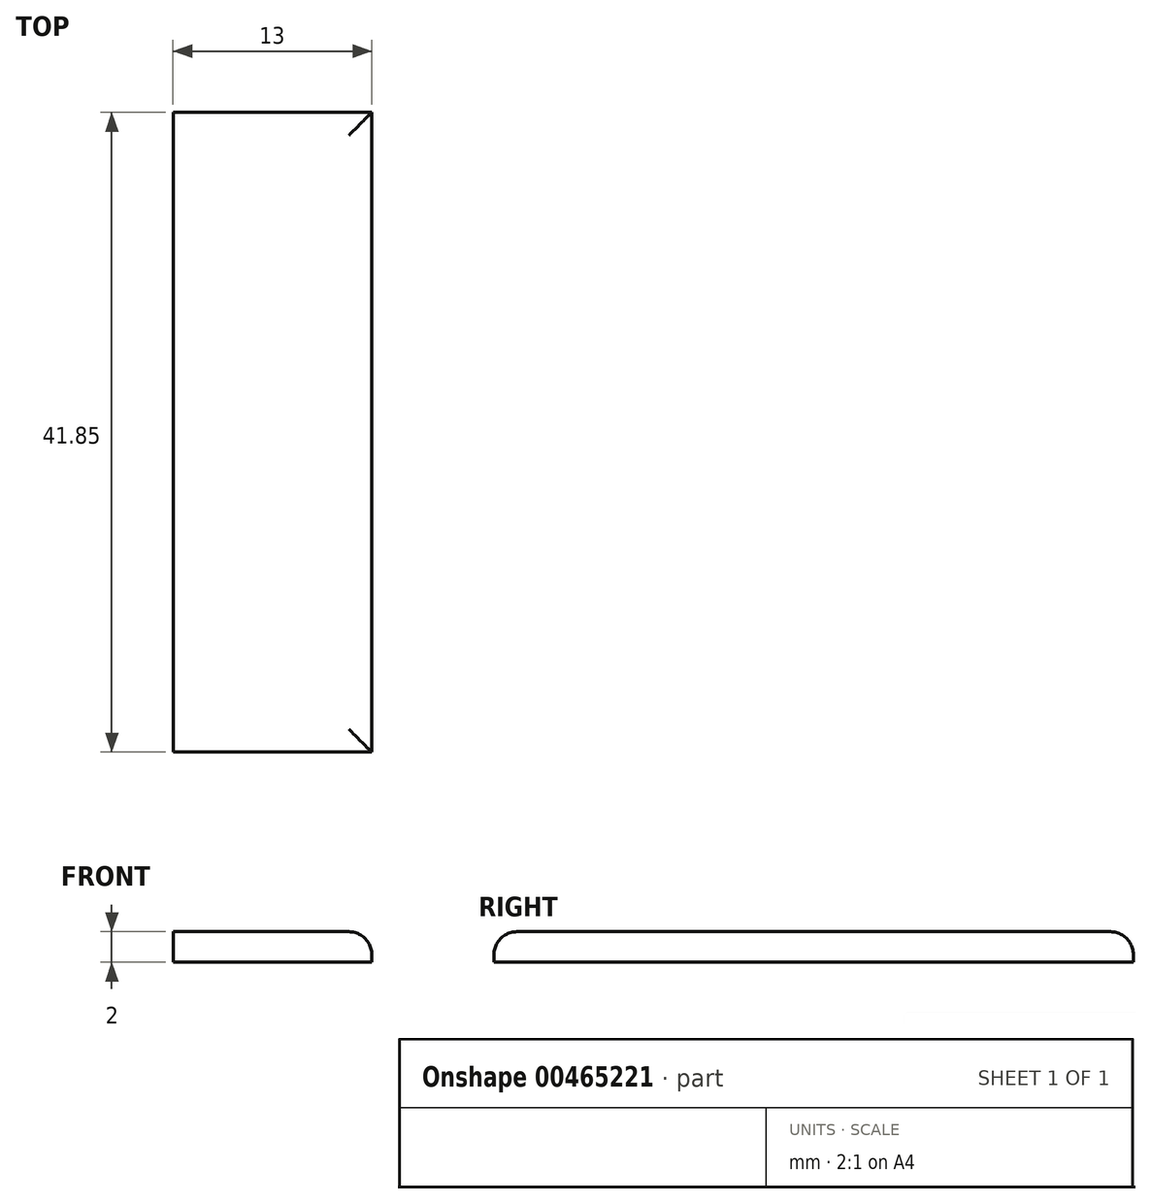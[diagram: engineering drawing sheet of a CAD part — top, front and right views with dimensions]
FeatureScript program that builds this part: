
annotation { "Feature Type Name" : "Feature", "Feature Type Description" : "" }
export const myFeature = defineFeature(function(context is Context, id is Id, definition is map)
    precondition{}
    {
        {
            var Q0;
            Q0=qCreatedBy(makeId("Top.planeOp"),FACE);
            var sketch = newSketch(context, id + "F0", { "sketchPlane" : qUnion([Q0])});
            skLineSegment(sketch, "E0.bottom", {"start": v(-8.26, 32.64) * mm, "end": v(4.74, 32.64) * mm});
            skLineSegment(sketch, "E0.top", {"start": v(-8.26, -9.2) * mm, "end": v(4.74, -9.2) * mm});
            skLineSegment(sketch, "E0.left", {"start": v(-8.26, 32.64) * mm, "end": v(-8.26, -9.2) * mm});
            skLineSegment(sketch, "E0.right", {"start": v(4.74, 32.64) * mm, "end": v(4.74, -9.2) * mm});
            skSolve(sketch);
        }
        {
            var Q0;
            Q0 = qSketchRegion(id + "F0", true);
            var Q1;
            Q1=makeQuery(id+"F0.imprint","IMPRINT",FACE,{"disambiguationData":[TD([[makeQuery(id+"F0.imprint","IMPRINT",EDGE,{"derivedFrom":sQuery(id+"F0.wireOp",EDGE,"E0.bottom")}),-1.0]])]});
            extrude(context, id + "F1", {"entities" : qUnion([Q0, Q1]), "depth" : 2 * mm});
        }
        {
            var Q0;
            Q0=makeQuery(id+"F1.opExtrude","CAP_EDGE",EDGE,{"disambiguationData":[OSD([sQuery(id+"F0.wireOp",EDGE,"E0.top")])],"isStart":false});
            var Q1;
            Q1=makeQuery(id+"F1.opExtrude","CAP_EDGE",EDGE,{"disambiguationData":[OSD([sQuery(id+"F0.wireOp",EDGE,"E0.right")])],"isStart":false});
            var Q2;
            Q2=makeQuery(id+"F1.opExtrude","CAP_EDGE",EDGE,{"disambiguationData":[OSD([sQuery(id+"F0.wireOp",EDGE,"E0.bottom")])],"isStart":false});
            fillet(context, id + "F2", {"entities" : qUnion([Q0, Q1, Q2]), "radius" : 1.5 * mm, "tangentPropagation" : true, "allowEdgeOverflow" : false});
        }
    });
